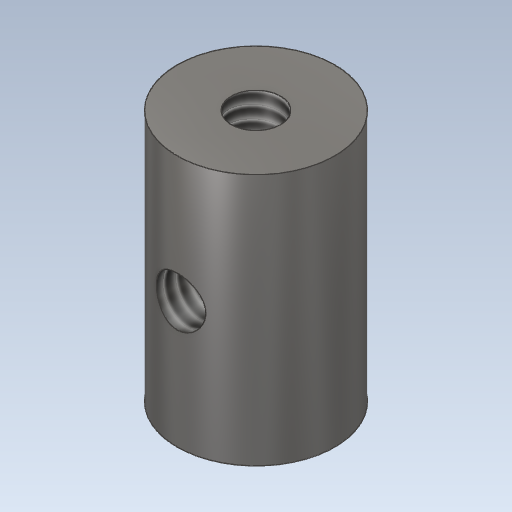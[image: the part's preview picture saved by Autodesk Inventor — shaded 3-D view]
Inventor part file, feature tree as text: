
AUTODESK INVENTOR PART (.ipt)
format: ipt  version: 2020 (Build 240168000, 168)  size: 156,672 bytes
history: native  units: in
note: dims shown in document units (in); Inventor stores cm internally (conversion verified against a paired STEP export)
features: sketch x3, hole x2, other x1, extrude x1, plane x1
ambient origin geometry x8: Origin, YZ Plane, XZ Plane, XY Plane, X Axis, Y Axis, Z Axis, Center Point
bodies: Solid1 (feature_tree)
feature tree (8):
  parser-record x1  (decoder bookkeeping rows leaked as tree rows — omitted from the tree; the rows remain in map.json)
  extrude  "Extrusion1"  Depth=1.0in TaperAngle=0.0deg
  hole  "Hole1"  [1 undecoded]
  plane  "Work Plane1"
  hole  "Hole2"  [1 undecoded]
  sketch  "Sketch1"  dims[d0=0.625in d1=1.0in d2=0.0in]
  sketch  "Sketch2"  dims[d3=0.196in d4=1.0in d5=0.385in d6=0.25in d7=0.5635in d8=0.75in d9=0.8108in d11=0.5in]
  sketch  "Sketch4"  dims[d12=0.196in d13=0.625in d14=0.385in d15=0.25in d16=0.5635in d17=0.75in d18=0.8108in]
note: 2 required parameter values undecoded (feature->parameter linkage not recoverable at this tier; creation-order binding heuristic only, values carry confidence <= 0.55)
note: 1 file-system path scrubbed to <path> (originals preserved in map.json)
